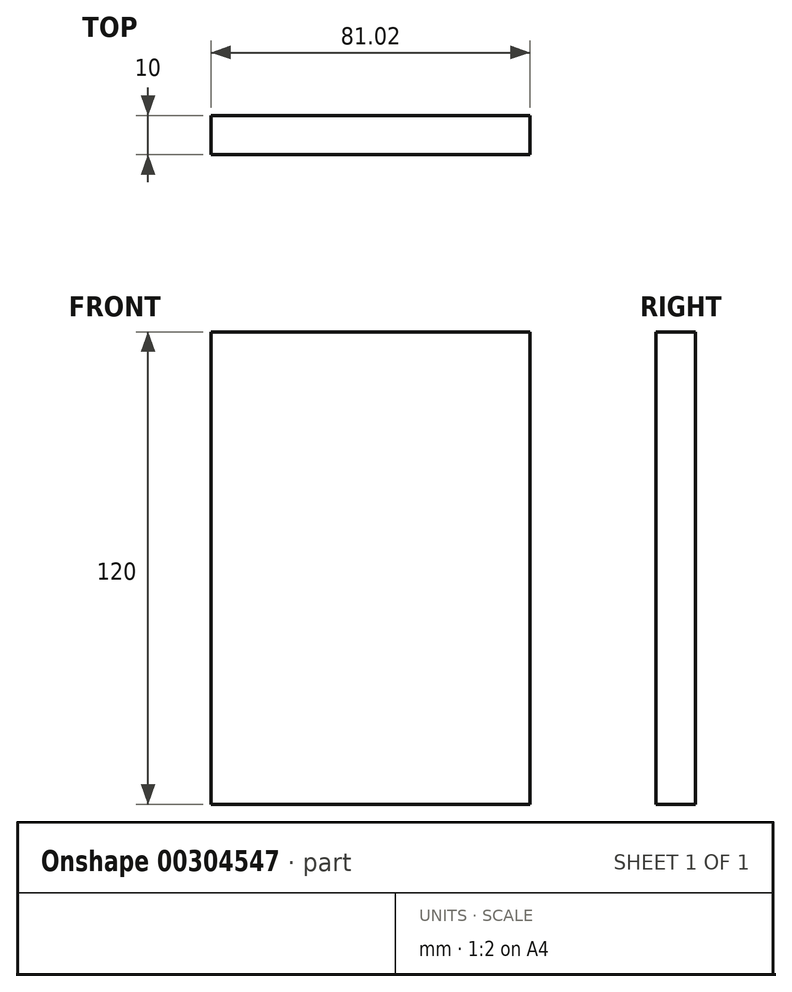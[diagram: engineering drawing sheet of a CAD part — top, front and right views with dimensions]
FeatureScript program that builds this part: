
annotation { "Feature Type Name" : "Feature", "Feature Type Description" : "" }
export const myFeature = defineFeature(function(context is Context, id is Id, definition is map)
    precondition{}
    {
        {
            var Q0;
            Q0=qCreatedBy(makeId("Front.planeOp"),FACE);
            var sketch = newSketch(context, id + "F0", { "sketchPlane" : qUnion([Q0])});
            skLineSegment(sketch, "E0.bottom", {"start": v(40.5, 60) * mm, "end": v(-40.5, 60) * mm});
            skLineSegment(sketch, "E0.top", {"start": v(40.5, -60) * mm, "end": v(-40.5, -60) * mm});
            skLineSegment(sketch, "E0.left", {"start": v(40.5, 60) * mm, "end": v(40.5, -60) * mm});
            skLineSegment(sketch, "E0.right", {"start": v(-40.5, 60) * mm, "end": v(-40.5, -60) * mm});
            skPoint(sketch, "E0.middle", {"position": v(0, 0) * mm});
            skSolve(sketch);
        }
        {
            var Q0;
            Q0 = qSketchRegion(id + "F0", true);
            extrude(context, id + "F1", {"entities" : qUnion([Q0]), "depth" : 10 * mm});
        }
    });
